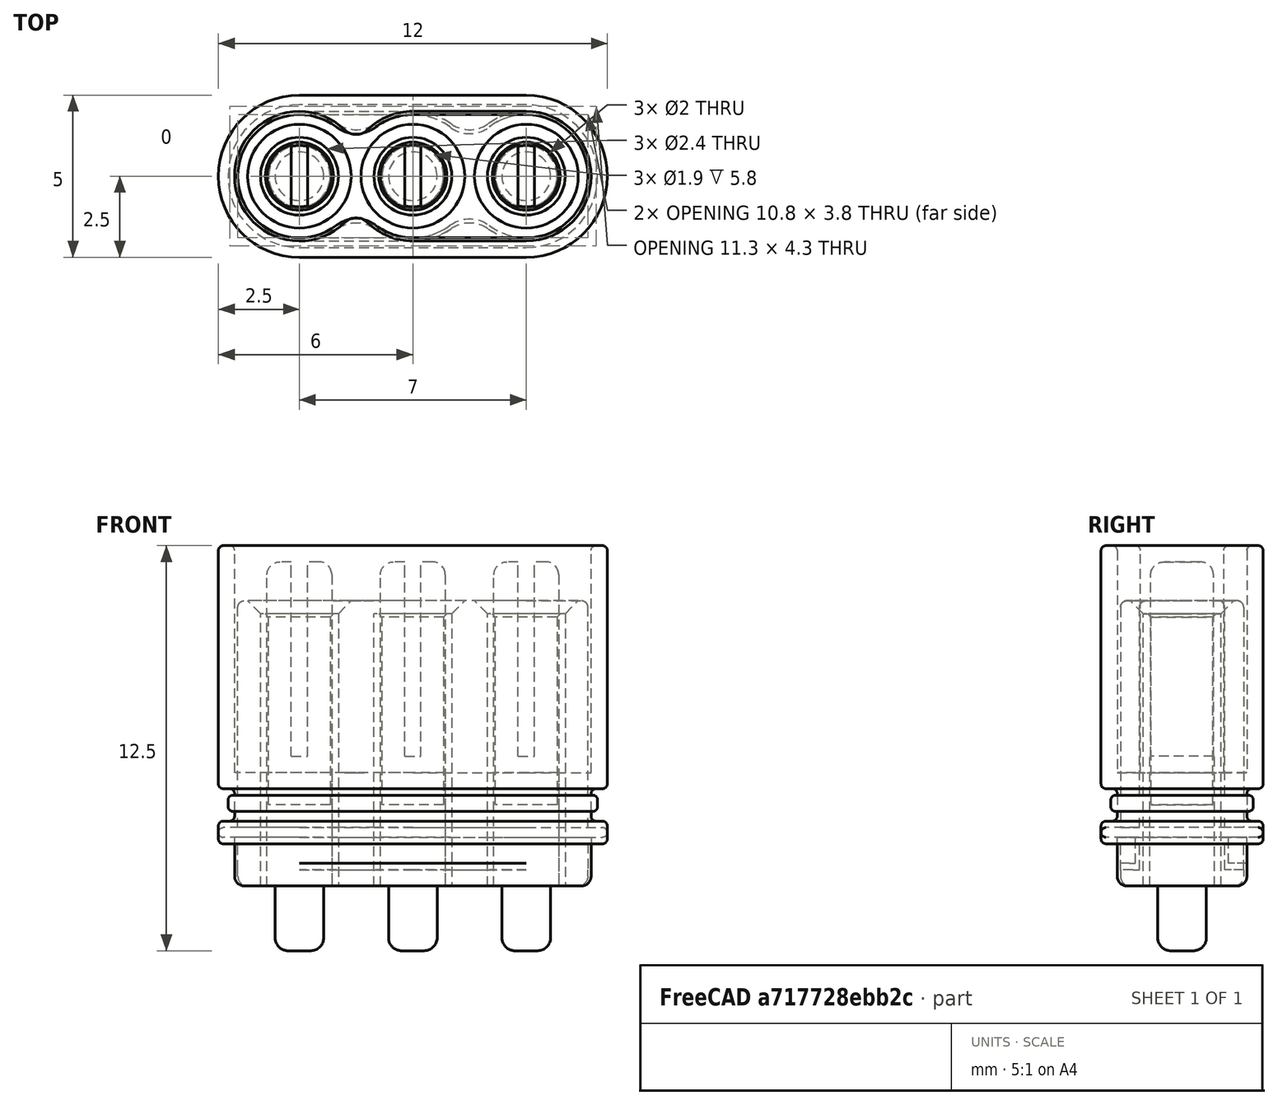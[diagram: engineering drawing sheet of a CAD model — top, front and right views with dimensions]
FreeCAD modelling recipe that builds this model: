
FCSTD DOCUMENT  (FreeCAD 0.16R6703 (Git))
Label: MR30
License: All rights reserved
LicenseURL: http://en.wikipedia.org/wiki/All_rights_reserved
objects: Part::Extrusion×23, Sketcher::SketchObject×14, Part::Fillet×14, Part::MultiFuse×10, Part::FeaturePython×4, Part::Cut×4, Part::Offset×3, Part::Compound×2, Part::Chamfer×2
note: 76 computed .brp shape members not serialized (recipe doc carries the construction recipe); baked Part::Feature solids carry a one-line shape summary decoded from their .brp

FEATURE [Sketcher::SketchObject] Sketch
  sketch-geometry (4):
    g0: ArcOfCircle CenterX=-3.5 CenterY=0 CenterZ=0 NormalX=0 NormalY=0 NormalZ=1 Radius=2.5 StartAngle=1.5708 EndAngle=4.71239
    g1: ArcOfCircle CenterX=3.5 CenterY=0 CenterZ=0 NormalX=0 NormalY=0 NormalZ=1 Radius=2.5 StartAngle=4.71239 EndAngle=7.85398
    g2: LineSegment StartX=-3.5 StartY=-2.5 StartZ=0 EndX=3.5 EndY=-2.5 EndZ=0
    g3: LineSegment StartX=-3.5 StartY=2.5 StartZ=0 EndX=3.5 EndY=2.5 EndZ=0
  constraints (10):
    c: Tangent(g0,g3) = 1.5708
    c: Tangent(g0,g2) = -1.5708
    c: Tangent(g2,g1) = -1.5708
    c: Tangent(g3,g1) = 1.5708
    c: Horizontal(g2)
    c: Equal(g0,g1)
    c: PointOnObject(g0,g-1)
    c: Symmetric(g1,g0,g-2)
    c: Distance(g3) = 7
    c: Radius(g1) = 2.5
FEATURE [Part::Extrusion] Extrude
  Base = -> Sketch
  Dir = (0,0,7.5)
  Solid = true
FEATURE [Part::Extrusion] Extrude001
  Base = -> Sketch
  Dir = (0,0,-2)
  Placement = pos=(0,0,0.5) rot=(0,0,1;0rad)
  Solid = true
FEATURE [Part::Offset] Offset
  Fill = false
  Intersection = false
  Join = 0
  Mode = 0
  SelfIntersection = false
  Source = -> Extrude001
  Value = -0.5
FEATURE [Part::Extrusion] Extrude002
  Base = -> Sketch
  Dir = (0,0,-0.5)
  Placement = pos=(0,0,-1) rot=(0,0,1;0rad)
  Solid = true
FEATURE [Sketcher::SketchObject] Sketch001
  Placement = pos=(0,0,-1.5) rot=(1,0,0;3.14159rad)
  sketch-geometry (1):
    g0: Circle CenterX=0 CenterY=0 CenterZ=0 NormalX=0 NormalY=0 NormalZ=1 Radius=2
  constraints (2):
    c: Coincident(g0,g-1)
    c: Radius(g0) = 2
FEATURE [Part::Extrusion] Extrude003
  Base = -> Sketch001
  Dir = (0,0,-0.8)
  Solid = true
FEATURE [Part::Extrusion] Extrude004
  Base = -> Sketch001
  Dir = (0,0,-0.8)
  Placement = pos=(-3.5,0,0) rot=(0,0,1;0rad)
  Solid = true
FEATURE [Part::Extrusion] Extrude005
  Base = -> Sketch001
  Dir = (0,0,-0.8)
  Placement = pos=(3.5,0,0) rot=(0,0,1;0rad)
  Solid = true
FEATURE [Part::MultiFuse] Fusion
  Shapes = -> [Extrude003,Extrude004,Extrude005]
FEATURE [Part::Fillet] Fillet
  Base = -> Fusion
  Edges = 4 edges r=1: [Edge2,Edge4,Edge6,Edge12]
FEATURE [Part::MultiFuse] Fusion001  label="body"
  Shapes = -> [Extrude,Offset,Extrude002]
FEATURE [Part::Fillet] Fillet001
  Base = -> Fusion001
  Edges = 5 edges r=0.15: [Edge9,Edge10,Edge15,Edge24,Edge27]
FEATURE [Part::Extrusion] Extrude006
  Base = -> Sketch
  Dir = (0,0,-1.7)
  Solid = true
FEATURE [Part::Offset] Offset001
  Fill = false
  Intersection = false
  Join = 0
  Mode = 0
  Placement = pos=(0,0,-1.8) rot=(0,0,1;0rad)
  SelfIntersection = false
  Source = -> Extrude006
  Value = -0.5
FEATURE [Part::Fillet] Fillet002
  Base = -> Offset001
  Edges = 1 edges r=0.3: [Edge8]
FEATURE [Part::MultiFuse] Fusion002  label="body001"
  Shapes = -> [Fillet,Fillet002,Fillet001]
FEATURE [Sketcher::SketchObject] Sketch002
  Placement = pos=(0,0,7.5) rot=(0,0,1;0rad)
  sketch-geometry (1):
    g0: Circle CenterX=-3.5 CenterY=0 CenterZ=0 NormalX=0 NormalY=0 NormalZ=1 Radius=2
  constraints (2):
    c: PointOnObject(g0,g-1)
    c: Radius(g0) = 2
FEATURE [Sketcher::SketchObject] Sketch003
  Placement = pos=(0,0,7.5) rot=(0,0,1;0rad)
  sketch-geometry (4):
    g0: ArcOfCircle CenterX=0 CenterY=0 CenterZ=0 NormalX=0 NormalY=0 NormalZ=1 Radius=2 StartAngle=1.5708 EndAngle=4.71239
    g1: ArcOfCircle CenterX=3.5 CenterY=0 CenterZ=0 NormalX=0 NormalY=0 NormalZ=1 Radius=2 StartAngle=4.71239 EndAngle=7.85398
    g2: LineSegment StartX=0 StartY=-2 StartZ=0 EndX=3.5 EndY=-2 EndZ=0
    g3: LineSegment StartX=0 StartY=2 StartZ=0 EndX=3.5 EndY=2 EndZ=0
  constraints (10):
    c: Tangent(g0,g3) = 1.5708
    c: Tangent(g0,g2) = -1.5708
    c: Tangent(g2,g1) = -1.5708
    c: Tangent(g3,g1) = 1.5708
    c: Horizontal(g2)
    c: Equal(g0,g1)
    c: PointOnObject(g0,g-1)
    c: DistanceX(g1) = 3.5
    c: Coincident(g0,g-1)
    c: Radius(g1) = 2
FEATURE [Part::Extrusion] Extrude007
  Base = -> Sketch002
  Dir = (0,0,-7)
  Solid = true
FEATURE [Part::Extrusion] Extrude008
  Base = -> Sketch003
  Dir = (0,0,-7)
  Solid = true
FEATURE [Part::MultiFuse] Fusion003
  Shapes = -> [Extrude008,Extrude007]
FEATURE [Part::Fillet] Fillet003
  Base = -> Fusion003
  Edges = 2 edges r=0.5: [Edge6,Edge20]
FEATURE [Sketcher::SketchObject] Sketch004
  Placement = pos=(0,0,7) rot=(0,0,1;0rad)
  sketch-geometry (1):
    g0: Circle CenterX=-3.5 CenterY=0 CenterZ=0 NormalX=0 NormalY=0 NormalZ=1 Radius=1
  constraints (3):
    c: PointOnObject(g0,g-1)
    c: DistanceX(g0) = -3.5
    c: Radius(g0) = 1
FEATURE [Part::Extrusion] Extrude009  label="pin"
  Base = -> Sketch004
  Dir = (0,0,-10)
  Solid = true
FEATURE [Part::FeaturePython] Array  # Draft array (typed FeaturePython)
  Angle = 360
  ArrayType = 0
  Axis = (0,0,1)
  Base = -> Extrude009
  Center = (0,0,0)
  Fuse = false
  IntervalAxis = (0,0,0)
  IntervalX = (3.5,0,0)
  IntervalY = (0,1,0)
  IntervalZ = (0,0,0)
  NumberPolar = 1
  NumberX = 3
  NumberY = 1
  NumberZ = 1
FEATURE [Part::MultiFuse] Fusion004
  Shapes = -> [Array,Fillet003]
FEATURE [Part::Cut] Cut  label="body002"
  Base = -> Fusion002
  Tool = -> Fusion004
FEATURE [Part::Fillet] Fillet004  label="body003"
  Base = -> Cut
  Edges = 2 edges r=0.15: [Edge117,Edge125]
FEATURE [Sketcher::SketchObject] Sketch005
  Placement = pos=(0,0,7) rot=(0,0,1;0rad)
  sketch-geometry (5):
    g0: LineSegment StartX=-3.75 StartY=1.62334 StartZ=0 EndX=-3.25 EndY=1.62334 EndZ=0
    g1: LineSegment StartX=-3.25 StartY=1.62334 StartZ=0 EndX=-3.25 EndY=-2 EndZ=0
    g2: LineSegment StartX=-3.25 StartY=-2 StartZ=0 EndX=-3.75 EndY=-2 EndZ=0
    g3: LineSegment StartX=-3.75 StartY=-2 StartZ=0 EndX=-3.75 EndY=1.62334 EndZ=0
    g4: LineSegment [constr] StartX=-3.5 StartY=0.232894 StartZ=0 EndX=-3.5 EndY=-0.5 EndZ=0
  constraints (12):
    c: Coincident(g0,g1)
    c: Coincident(g1,g2)
    c: Coincident(g2,g3)
    c: Coincident(g3,g0)
    c: Horizontal(g0)
    c: Horizontal(g2)
    c: Vertical(g1)
    c: Vertical(g3)
    c: Vertical(g4)
    c: DistanceX(g4) = -3.5
    c: Symmetric(g0,g0,g4)
    c: Distance(g0) = 0.5
FEATURE [Part::Extrusion] Extrude010
  Base = -> Sketch005
  Dir = (0,0,-6)
  Solid = true
FEATURE [Part::Fillet] Fillet005  label="pin001"
  Base = -> Extrude009
  Edges = 1 edges r=0.4: [Edge2]
FEATURE [Part::Cut] Cut001
  Base = -> Fillet005
  Tool = -> Extrude010
FEATURE [Sketcher::SketchObject] Sketch006
  Placement = pos=(0,0,-3) rot=(1,0,0;3.14159rad)
  sketch-geometry (1):
    g0: Circle CenterX=-3.5 CenterY=0 CenterZ=0 NormalX=0 NormalY=0 NormalZ=1 Radius=0.75
  constraints (3):
    c: PointOnObject(g0,g-1)
    c: DistanceX(g0) = -3.5
    c: Radius(g0) = 0.75
FEATURE [Part::Extrusion] Extrude011
  Base = -> Sketch006
  Dir = (0,0,-2)
  Solid = true
FEATURE [Part::Fillet] Fillet006
  Base = -> Extrude011
  Edges = 1 edges r=0.4: [Edge3]
FEATURE [Part::MultiFuse] Fusion005  label="pin002"
  Shapes = -> [Fillet006,Cut001]
FEATURE [Part::FeaturePython] Array001  label="pins"  # Draft array (typed FeaturePython)
  Angle = 360
  ArrayType = 0
  Axis = (0,0,1)
  Base = -> Fusion005
  Center = (0,0,0)
  Fuse = false
  IntervalAxis = (0,0,0)
  IntervalX = (3.5,0,0)
  IntervalY = (0,1,0)
  IntervalZ = (0,0,0)
  NumberPolar = 1
  NumberX = 3
  NumberY = 1
  NumberZ = 1
FEATURE [Part::Compound] Compound  label="MR30PB-M"
  Links = -> [Fillet004,Array001]
  Placement = pos=(0,0,3) rot=(0,0,1;0rad)
FEATURE [Sketcher::SketchObject] Sketch007
  Placement = pos=(0,0,7.5) rot=(0,0,1;0rad)
  sketch-geometry (1):
    g0: Circle CenterX=-3.5 CenterY=0 CenterZ=0 NormalX=0 NormalY=0 NormalZ=1 Radius=1.9
  constraints (3):
    c: PointOnObject(g0,g-1)
    c: Radius(g0) = 1.9
    c: DistanceX(g0) = -3.5
FEATURE [Sketcher::SketchObject] Sketch008
  Placement = pos=(0,0,7.5) rot=(0,0,1;0rad)
  sketch-geometry (4):
    g0: ArcOfCircle CenterX=0 CenterY=0 CenterZ=0 NormalX=0 NormalY=0 NormalZ=1 Radius=1.9 StartAngle=1.5708 EndAngle=4.71239
    g1: ArcOfCircle CenterX=3.5 CenterY=0 CenterZ=0 NormalX=0 NormalY=0 NormalZ=1 Radius=1.9 StartAngle=4.71239 EndAngle=7.85398
    g2: LineSegment StartX=0 StartY=-1.9 StartZ=0 EndX=3.5 EndY=-1.9 EndZ=0
    g3: LineSegment StartX=0 StartY=1.9 StartZ=0 EndX=3.5 EndY=1.9 EndZ=0
  constraints (10):
    c: Tangent(g0,g3) = 1.5708
    c: Tangent(g0,g2) = -1.5708
    c: Tangent(g2,g1) = -1.5708
    c: Tangent(g3,g1) = 1.5708
    c: Horizontal(g2)
    c: Equal(g0,g1)
    c: PointOnObject(g0,g-1)
    c: DistanceX(g1) = 3.5
    c: Coincident(g0,g-1)
    c: Radius(g1) = 1.9
FEATURE [Part::Extrusion] Extrude012
  Base = -> Sketch007
  Dir = (0,0,-7)
  Solid = true
FEATURE [Part::Extrusion] Extrude013
  Base = -> Sketch008
  Dir = (0,0,-7)
  Solid = true
FEATURE [Sketcher::SketchObject] Sketch009
  Placement = pos=(0,0,7) rot=(0,0,1;0rad)
  sketch-geometry (1):
    g0: Circle CenterX=-3.5 CenterY=0 CenterZ=0 NormalX=0 NormalY=0 NormalZ=1 Radius=1.2
  constraints (3):
    c: PointOnObject(g0,g-1)
    c: DistanceX(g0) = -3.5
    c: Radius(g0) = 1.2
FEATURE [Part::Extrusion] Extrude014  label="pin003"
  Base = -> Sketch009
  Dir = (0,0,-10)
  Solid = true
FEATURE [Part::FeaturePython] Array002  # Draft array (typed FeaturePython)
  Angle = 360
  ArrayType = 0
  Axis = (0,0,1)
  Base = -> Extrude014
  Center = (0,0,0)
  Fuse = false
  IntervalAxis = (0,0,0)
  IntervalX = (3.5,0,0)
  IntervalY = (0,1,0)
  IntervalZ = (0,0,0)
  NumberPolar = 1
  NumberX = 3
  NumberY = 1
  NumberZ = 1
FEATURE [Part::Extrusion] Extrude015  label="pin004"
  Base = -> Sketch009
  Dir = (0,0,-8.4)
  Placement = pos=(0,0,-1.4) rot=(0,0,1;0rad)
  Solid = true
FEATURE [Part::Extrusion] Extrude017
  Base = -> Sketch
  Dir = (0,0,-0.5)
  Placement = pos=(0,0,-1) rot=(0,0,1;0rad)
  Solid = true
FEATURE [Part::Fillet] Fillet011
  Base = -> Extrude017
  Edges = 2 edges r=0.15: [Edge6,Edge7]
FEATURE [Sketcher::SketchObject] Sketch010
  Placement = pos=(0,0,7.2) rot=(0,0,1;0rad)
  sketch-geometry (1):
    g0: Circle CenterX=-3.5 CenterY=0 CenterZ=0 NormalX=0 NormalY=0 NormalZ=1 Radius=0.95
  constraints (3):
    c: PointOnObject(g0,g-1)
    c: DistanceX(g0) = -3.5
    c: Radius(g0) = 0.95
FEATURE [Part::Extrusion] Extrude016
  Base = -> Sketch010
  Dir = (0,0,-7.5)
  Solid = true
FEATURE [Part::Cut] Cut003  label="pinFemale"
  Base = -> Extrude015
  Tool = -> Extrude016
FEATURE [Sketcher::SketchObject] Sketch011
  sketch-geometry (4):
    g0: ArcOfCircle CenterX=-3.5 CenterY=0 CenterZ=0 NormalX=0 NormalY=0 NormalZ=1 Radius=2.2 StartAngle=1.5708 EndAngle=4.71239
    g1: ArcOfCircle CenterX=3.5 CenterY=0 CenterZ=0 NormalX=0 NormalY=0 NormalZ=1 Radius=2.2 StartAngle=4.71239 EndAngle=7.85398
    g2: LineSegment StartX=-3.5 StartY=-2.2 StartZ=0 EndX=3.5 EndY=-2.2 EndZ=0
    g3: LineSegment StartX=-3.5 StartY=2.2 StartZ=0 EndX=3.5 EndY=2.2 EndZ=0
  constraints (10):
    c: Tangent(g0,g3) = 1.5708
    c: Tangent(g0,g2) = -1.5708
    c: Tangent(g2,g1) = -1.5708
    c: Tangent(g3,g1) = 1.5708
    c: Horizontal(g2)
    c: Equal(g0,g1)
    c: PointOnObject(g0,g-1)
    c: Symmetric(g1,g0,g-2)
    c: Distance(g3) = 7
    c: Radius(g1) = 2.2
FEATURE [Part::Extrusion] Extrude018
  Base = -> Sketch011
  Dir = (0,0,-0.5)
  Placement = pos=(0,0,-1) rot=(0,0,1;0rad)
  Solid = true
FEATURE [Part::Fillet] Fillet012
  Base = -> Extrude018
  Edges = 2 edges r=0.15: [Edge6,Edge7]
  Placement = pos=(0,0,1) rot=(0,0,1;0rad)
FEATURE [Sketcher::SketchObject] Sketch012
  Placement = pos=(0,0,-1.5) rot=(1,0,0;3.14159rad)
  sketch-geometry (1):
    g0: Circle CenterX=0 CenterY=0 CenterZ=0 NormalX=0 NormalY=0 NormalZ=1 Radius=1.9
  constraints (2):
    c: Coincident(g0,g-1)
    c: Radius(g0) = 1.9
FEATURE [Part::Extrusion] Extrude019
  Base = -> Sketch012
  Dir = (0,0,-0.8)
  Solid = true
FEATURE [Part::Extrusion] Extrude020
  Base = -> Sketch012
  Dir = (0,0,-0.8)
  Placement = pos=(-3.5,0,0) rot=(0,0,1;0rad)
  Solid = true
FEATURE [Part::Extrusion] Extrude021
  Base = -> Sketch012
  Dir = (0,0,-0.8)
  Placement = pos=(3.5,0,0) rot=(0,0,1;0rad)
  Solid = true
FEATURE [Part::MultiFuse] Fusion008
  Shapes = -> [Extrude019,Extrude020,Extrude021]
FEATURE [Part::Fillet] Fillet013
  Base = -> Fusion008
  Edges = 4 edges r=1: [Edge2,Edge4,Edge6,Edge12]
FEATURE [Part::Offset] Offset002
  Fill = false
  Intersection = false
  Join = 0
  Mode = 0
  Placement = pos=(0,0,-1.7) rot=(0,0,1;0rad)
  SelfIntersection = false
  Source = -> Extrude006
  Value = -0.6
FEATURE [Part::Fillet] Fillet014
  Base = -> Offset002
  Edges = 1 edges r=0.3: [Edge3]
FEATURE [Part::MultiFuse] Fusion009
  Shapes = -> [Extrude013,Extrude012]
FEATURE [Part::Fillet] Fillet015
  Base = -> Fusion009
  Edges = 2 edges r=1: [Edge6,Edge20]
FEATURE [Part::Fillet] Fillet016
  Base = -> Fillet015
  Edges = 1 edges r=0.2: [Edge10]
  Placement = pos=(0,0,-1.5) rot=(0,0,1;0rad)
FEATURE [Part::MultiFuse] Fusion010  label="bodyFemale"
  Shapes = -> [Fillet016,Fillet012,Fillet014,Fillet013,Fillet011]
FEATURE [Part::Cut] Cut004
  Base = -> Fusion010
  Tool = -> Array002
FEATURE [Part::Chamfer] Chamfer  label="bodyFemale001"
  Base = -> Cut004
  Edges = 3 edges r=0.4: [Edge16,Edge18,Edge20]
FEATURE [Part::Chamfer] Chamfer001  label="pinFemale001"
  Base = -> Cut003
  Edges = 1 edges r=0.1: [Edge4]
FEATURE [Sketcher::SketchObject] Sketch013
  Placement = pos=(0,0,-2.8) rot=(1,0,0;3.14159rad)
  sketch-geometry (1):
    g0: Circle CenterX=-3.5 CenterY=0 CenterZ=0 NormalX=0 NormalY=0 NormalZ=1 Radius=0.75
  constraints (3):
    c: PointOnObject(g0,g-1)
    c: Radius(g0) = 0.75
    c: DistanceX(g0) = -3.5
FEATURE [Part::Extrusion] Extrude022
  Base = -> Sketch013
  Dir = (0,0,-2)
  Solid = true
FEATURE [Part::Fillet] Fillet017
  Base = -> Extrude022
  Edges = 1 edges r=0.4: [Edge3]
FEATURE [Part::MultiFuse] Fusion011  label="pinFemale002"
  Shapes = -> [Chamfer001,Fillet017]
FEATURE [Part::FeaturePython] Array003  # Draft array (typed FeaturePython)
  Angle = 360
  ArrayType = 0
  Axis = (0,0,1)
  Base = -> Fusion011
  Center = (0,0,0)
  Fuse = false
  IntervalAxis = (0,0,0)
  IntervalX = (3.5,0,0)
  IntervalY = (0,1,0)
  IntervalZ = (0,0,0)
  NumberPolar = 1
  NumberX = 3
  NumberY = 1
  NumberZ = 1
FEATURE [Part::Compound] Compound001  label="MR30PB-FB"
  Links = -> [Chamfer,Array003]
  Placement = pos=(0,0,2.8) rot=(0,0,1;0rad)
